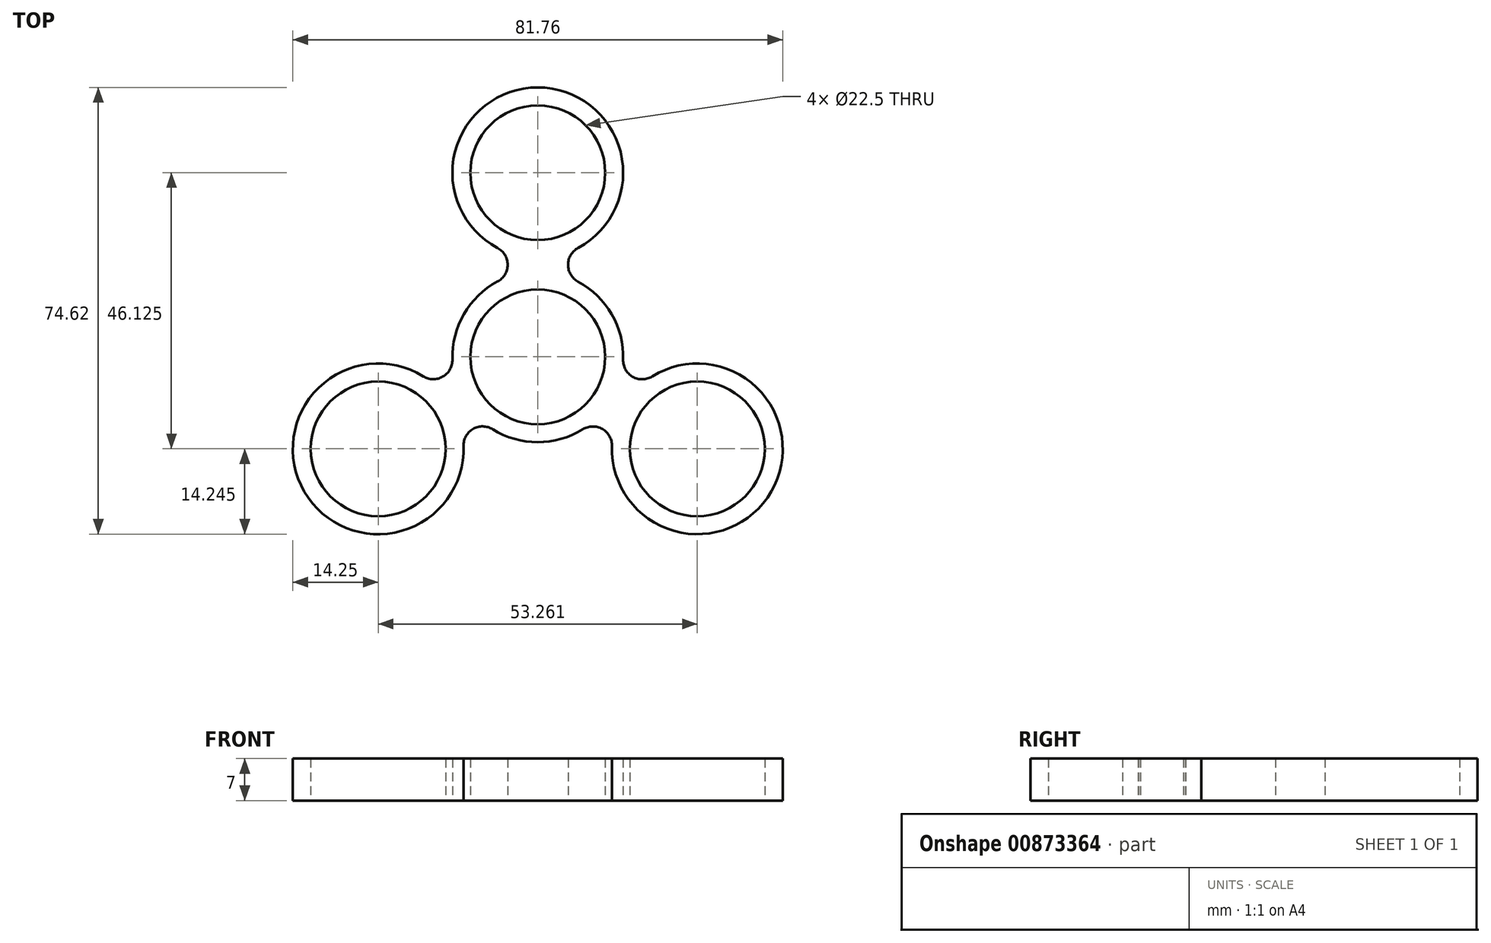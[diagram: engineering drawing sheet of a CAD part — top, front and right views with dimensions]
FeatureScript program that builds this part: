
annotation { "Feature Type Name" : "Feature", "Feature Type Description" : "" }
export const myFeature = defineFeature(function(context is Context, id is Id, definition is map)
    precondition{}
    {
        {
            var Q0;
            Q0=qCreatedBy(makeId("Top.planeOp"),FACE);
            var sketch = newSketch(context, id + "F0", { "sketchPlane" : qUnion([Q0])});
            skCircle(sketch, "E0", {"center": v(0, 0) * mm, "radius": 11.25 * mm});
            skCircle(sketch, "E1", {"center": v(0, 0) * mm, "radius": 45 * mm, "construction": true});
            skArc(sketch, "E2", {"start": v(6.75, 18.2) * mm, "mid": v(-0.02, 45) * mm, "end": v(-6.72, 18.18) * mm});
            skArc(sketch, "E3", {"start": v(-6.72, 12.57) * mm, "mid": v(-12.33, 7.14) * mm, "end": v(-14.24, -0.43) * mm});
            skCircle(sketch, "E4", {"center": v(0, 30.75) * mm, "radius": 11.25 * mm});
            skCircle(sketch, "E5.1.0", {"center": v(-26.63, -15.37) * mm, "radius": 11.25 * mm});
            skArc(sketch, "E5.1.1", {"start": v(-19.13, -3.26) * mm, "mid": v(-38.96, -22.51) * mm, "end": v(-12.39, -14.9) * mm});
            skCircle(sketch, "E5.2.0", {"center": v(26.63, -15.37) * mm, "radius": 11.25 * mm});
            skArc(sketch, "E5.2.1", {"start": v(12.39, -14.94) * mm, "mid": v(38.98, -22.49) * mm, "end": v(19.1, -3.27) * mm});
            skArc(sketch, "E6", {"start": v(-6.72, 12.57) * mm, "mid": v(-5.04, 15.37) * mm, "end": v(-6.72, 18.18) * mm});
            skArc(sketch, "E7", {"start": v(6.75, 18.2) * mm, "mid": v(5.06, 15.37) * mm, "end": v(6.75, 12.55) * mm});
            skArc(sketch, "E8.1.0", {"start": v(-7.52, -12.1) * mm, "mid": v(-10.8, -12.05) * mm, "end": v(-12.39, -14.9) * mm});
            skArc(sketch, "E8.1.1", {"start": v(-19.13, -3.26) * mm, "mid": v(-15.84, -3.3) * mm, "end": v(-14.24, -0.43) * mm});
            skArc(sketch, "E8.2.0", {"start": v(14.24, -0.47) * mm, "mid": v(15.83, -3.33) * mm, "end": v(19.1, -3.27) * mm});
            skArc(sketch, "E8.2.1", {"start": v(12.39, -14.94) * mm, "mid": v(10.79, -12.07) * mm, "end": v(7.5, -12.12) * mm});
            skArc(sketch, "E9.trimOffspring", {"start": v(-7.52, -12.1) * mm, "mid": v(-0.02, -14.25) * mm, "end": v(7.5, -12.12) * mm});
            skArc(sketch, "E10.trimOffspring", {"start": v(14.24, -0.47) * mm, "mid": v(12.35, 7.11) * mm, "end": v(6.75, 12.55) * mm});
            skSolve(sketch);
        }
        {
            var Q0;
            Q0=makeQuery(id+"F0.imprint","IMPRINT",FACE,{"disambiguationData":[TD([[makeQuery(id+"F0.imprint","IMPRINT",EDGE,{"derivedFrom":sQuery(id+"F0.wireOp",EDGE,"E0")}),-1.0]])]});
            extrude(context, id + "F1", {"entities" : qUnion([Q0]), "depth" : 7 * mm, "offsetDistance" : 25 * mm});
        }
    });
